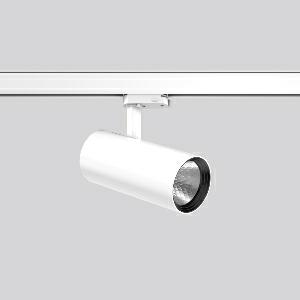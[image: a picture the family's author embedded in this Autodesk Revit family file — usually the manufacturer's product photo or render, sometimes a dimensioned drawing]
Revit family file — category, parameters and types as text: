
# Revit family: deecos_s_mini_742195_002_3_76_a6a4
name_source: partatom
category: Lighting Fixtures
units: mm (PartAtom-declared; Revit-internal decimal feet)

## family parameters
Cut with Voids When Loaded = No
Host = Face
Light Source = No
Part Type = Normal
Room Calculation Point = No
Round Connector Dimension = Use Diameter
Shared = No

## types (1)
- DEECOS S mini (1 x LED Modul 935, 2600 lm, 3500)
    Apparent Load = 20 VA
    Approval mark = CE
    CIE Flux Codes = 100 100 100 100 100
    Color Rendering = 92
    Color Temperature = 3500
    Default Elevation = 1800 mm
    Description = Series: DEECOS S mini
LED surface-mounted projector in modern design with no visible cooling ribs. Housing: die-cast aluminium, powder-coated. Rotation range: 356°. Swivel range: 90°. Black plastic ring and recessed LED to prevent glare from the side. Optical assembly with reflector made of MIRO-Silver with 98% total light reflection for outstanding efficiency - can be changed without tools. Best colour rendering index Ra>90. With adapter for RZB 3-circuit DALI tracks. Suitable for Track on ceiling, Wall track. High quality converter without flickering and stroboscopic effect. The following accessories can be mounted without use of tools: interchangeable lenses, decorative glasses, honeycomb louvre, clear and frosted diffusers, white interchangeable plastic ring. 
Colour: traffic white, matt (RAL 9016)
Diameter: 87 mm
Height: 214 mm
Lamp: LED
Socket: without socket
Colour temperature: 3500K
Colour rendering index (CRI): 92
System power: 20 W
Rated luminous flux: 2600 lm
Luminous efficiency: 130 lm/W
Control gear: Converter, dimmable, DALI
Protection class: I
Type of protection: IP 20
    Height = 214 mm
    Lamp = 1 x LED Modul 935
    Lamp Light Flux = 2600 lm
    Lamp count = 1
    Length = 87 mm
    Lifetime = 50000 h
    Luminous efficacy = 130 lm/W
    Manufacturer = RZB
    ModVariant = No
    Model = 742195.002.3.76
    Mounting Place = Ceiling
    Mounting Type = Rail mounted
    Number of Poles = 1
    OnlyDefault = Yes
    Power Factor = 1
    Product Name = DEECOS S mini
    Product group = Track mounted projectors
    ProductGroupID = 301
    Protection Class = Protection class I
    Protection Degree = IP 20
    RLX_Detail_Level = 1
    RLX_Emergency_Light_Flux = 0 lm
    RLX_Emergency_Type = 0
    RLX_Emergency_Type_DB = No
    RlxData = <blob elided: 35025 chars, md5=180e6b39>
    Socket = socket
    Standby Power = 0 W
    System Light Flux = 2600 lm
    System Power = 20 W
    Type Comments = Product without accessories
    Type Image = 741926.002.jpg
    URL = http://relux.com
    VarID = ---
    Voltage = 230 V
    Voltage Range = 220-240 V
    Weight = 0.00 kg
    Width = 0 mm  [stored 0 ft]

note: [stored X ft] marks values corroborated as IEEE doubles in the binary element streams (Revit-internal decimal feet)

## geometry (parser evidence)
native form markers: Blend x4, Sweep x12
no freeform markers — native parametric forms only
